# Revit family: Doors_Industrial_Wayne-Dalton_Roll-Up-Sheet-Mini-Storage-Doors-Model-DS-75_
name_source: partatom
category: Specialty Equipment
units: mm (PartAtom-declared; Revit-internal decimal feet)

## family parameters
Always vertical = Yes
Cut with Voids When Loaded = No
Host = Wall
OmniClass Number = 23.30.10.21.34
OmniClass Title = Industrial Doors
Part Type = Normal
Room Calculation Point = No
Round Connector Dimension = Use Diameter
Shared = No

## types (1)
- Manual push-up
    BR Shaft Distance = 4 1/2"
    Description = Model DS-75 Light Commercial Mini Roll-Up Door (R-Value 4.0 with optional insulation)
    Finish Material = Metal - Wayne Dalton - Galvanized Steel
    Manufacturer = Wayne Dalton
    Model = DS-75
    Product Guid = 8cb6006f-850d-402b-b535-a3554302deac
    Product Page URL = https://www.wayne-dalton.com
    Product data url = https://www.bimobject.com
    Slat to Wall Offset = 1 1/2"
    URL = https://www.wayne-dalton.com
    Wall Closure = By host

## geometry (parser evidence)
native form markers: Sweep x14
no freeform markers — native parametric forms only
